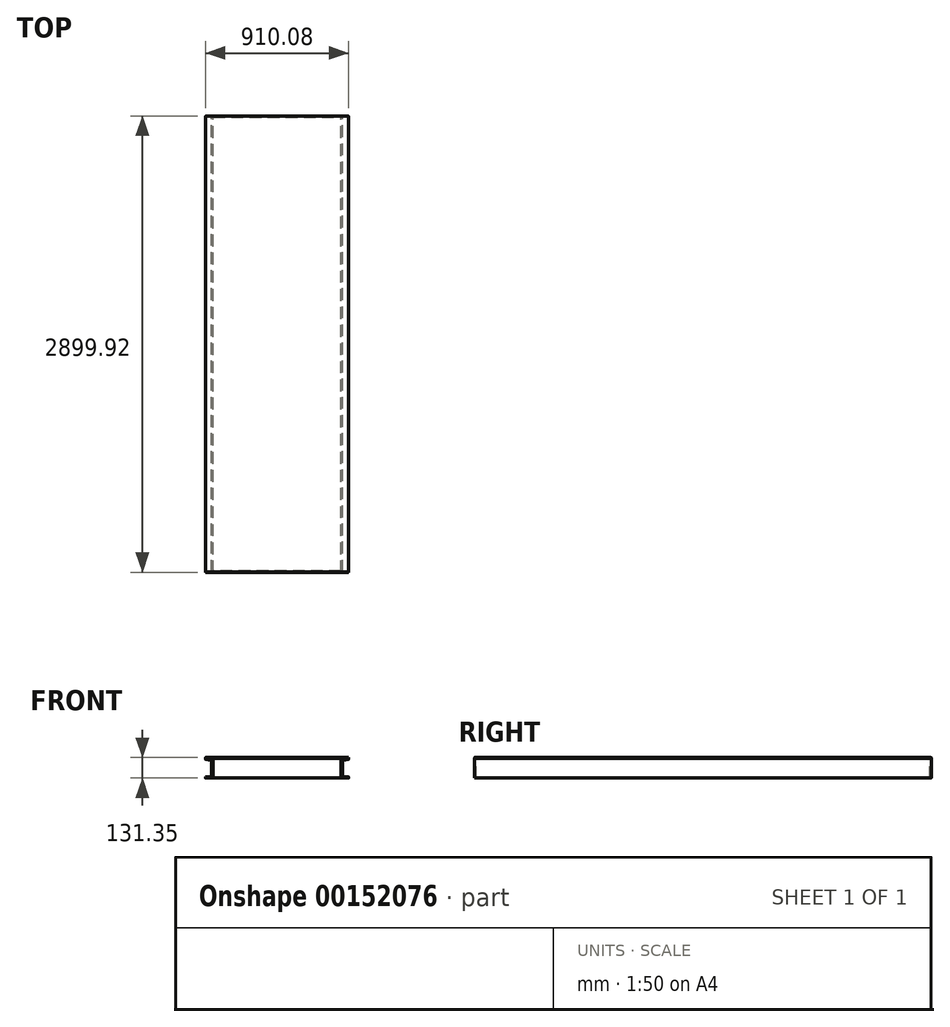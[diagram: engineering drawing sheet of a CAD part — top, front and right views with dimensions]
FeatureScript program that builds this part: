
annotation { "Feature Type Name" : "Feature", "Feature Type Description" : "" }
export const myFeature = defineFeature(function(context is Context, id is Id, definition is map)
    precondition{}
    {
        {
            var Q0;
            Q0=qCreatedBy(makeId("Front.planeOp"),FACE);
            var sketch = newSketch(context, id + "F0", { "sketchPlane" : qUnion([Q0])});
            skLineSegment(sketch, "E0", {"start": v(0, 0) * mm, "end": v(-50, 0) * mm});
            skLineSegment(sketch, "E1", {"start": v(0, 0) * mm, "end": v(0, 125) * mm});
            skLineSegment(sketch, "E2", {"start": v(0, 125) * mm, "end": v(-50, 125) * mm});
            skLineSegment(sketch, "E3", {"start": v(-50, 125) * mm, "end": v(-50, 117.2) * mm});
            skLineSegment(sketch, "E4", {"start": v(-50, 117.2) * mm, "end": v(-10, 113) * mm});
            skLineSegment(sketch, "E5", {"start": v(-10, 113) * mm, "end": v(-10, 12) * mm});
            skLineSegment(sketch, "E6", {"start": v(-50, 0) * mm, "end": v(-50, 7.8) * mm});
            skLineSegment(sketch, "E7", {"start": v(-50, 7.8) * mm, "end": v(-10, 12) * mm});
            skLineSegment(sketch, "E8", {"start": v(405, 151.35) * mm, "end": v(405, -34.02) * mm});
            skLineSegment(sketch, "E9.MirrorCS", {"start": v(860, 125) * mm, "end": v(860, 117.2) * mm});
            skLineSegment(sketch, "E10.MirrorCS", {"start": v(860, 0) * mm, "end": v(860, 7.8) * mm});
            skLineSegment(sketch, "E11.MirrorCS", {"start": v(860, 117.2) * mm, "end": v(820, 113) * mm});
            skLineSegment(sketch, "E12.MirrorCS", {"start": v(860, 7.8) * mm, "end": v(820, 12) * mm});
            skLineSegment(sketch, "E13.MirrorCS", {"start": v(810, 125) * mm, "end": v(860, 125) * mm});
            skLineSegment(sketch, "E14.MirrorCS", {"start": v(810, 0) * mm, "end": v(860, 0) * mm});
            skLineSegment(sketch, "E15.MirrorCS", {"start": v(810, 0) * mm, "end": v(810, 125) * mm});
            skLineSegment(sketch, "E16.MirrorCS", {"start": v(820, 113) * mm, "end": v(820, 12) * mm});
            skSolve(sketch);
        }
        {
            var Q0;
            Q0 = qSketchRegion(id + "F0", true);
            extrude(context, id + "F1", {"entities" : qUnion([Q0]), "depth" : 2899.92 * mm});
        }
        {
            var Q0;
            Q0=makeQuery(id+"F1.opExtrude","SWEPT_FACE",FACE,{"disambiguationData":[OSD([sQuery(id+"F0.wireOp",EDGE,"E2")])]});
            var sketch = newSketch(context, id + "F2", { "sketchPlane" : qUnion([Q0])});
            skLineSegment(sketch, "E17.bottom", {"start": v(-50, 0) * mm, "end": v(860.08, 0) * mm});
            skLineSegment(sketch, "E17.top", {"start": v(-50, -2899.92) * mm, "end": v(860.08, -2899.92) * mm});
            skLineSegment(sketch, "E17.left", {"start": v(-50, 0) * mm, "end": v(-50, -2899.92) * mm});
            skLineSegment(sketch, "E17.right", {"start": v(860.08, 0) * mm, "end": v(860.08, -2899.92) * mm});
            skSolve(sketch);
        }
        {
            var Q0;
            Q0 = qSketchRegion(id + "F2", true);
            extrude(context, id + "F3", {"entities" : qUnion([Q0]), "depth" : 6.35 * mm});
        }
        {
            var Q0;
            Q0=makeQuery(id+"F3.opExtrude","CAP_FACE",FACE,{"disambiguationData":[OSD([sQuery(id+"F2.wireOp",EDGE,"E17.bottom"),sQuery(id+"F2.wireOp",EDGE,"E17.top"),sQuery(id+"F2.wireOp",EDGE,"E17.left"),sQuery(id+"F2.wireOp",EDGE,"E17.right")])],"isStart":true});
            var sketch = newSketch(context, id + "F4", { "sketchPlane" : qUnion([Q0])});
            skLineSegment(sketch, "E18.bottom", {"start": v(810.22, 2899.92) * mm, "end": v(0, 2899.92) * mm});
            skLineSegment(sketch, "E18.top", {"start": v(810.22, 2891.42) * mm, "end": v(0, 2891.42) * mm});
            skLineSegment(sketch, "E18.left", {"start": v(810.22, 2899.92) * mm, "end": v(810.22, 2891.42) * mm});
            skLineSegment(sketch, "E18.right", {"start": v(0, 2899.92) * mm, "end": v(0, 2891.42) * mm});
            skSolve(sketch);
        }
        {
            var Q0;
            Q0 = qSketchRegion(id + "F4", true);
            extrude(context, id + "F5", {"entities" : qUnion([Q0]), "depth" : 125 * mm});
        }
        {
            var Q0;
            Q0=makeQuery(id+"F3.opExtrude","CAP_FACE",FACE,{"disambiguationData":[OSD([sQuery(id+"F2.wireOp",EDGE,"E17.bottom"),sQuery(id+"F2.wireOp",EDGE,"E17.top"),sQuery(id+"F2.wireOp",EDGE,"E17.left"),sQuery(id+"F2.wireOp",EDGE,"E17.right")])],"isStart":true});
            var sketch = newSketch(context, id + "F6", { "sketchPlane" : qUnion([Q0])});
            skLineSegment(sketch, "E19.bottom", {"start": v(0, 0) * mm, "end": v(809.94, 0) * mm});
            skLineSegment(sketch, "E19.top", {"start": v(0, 8.5) * mm, "end": v(809.94, 8.5) * mm});
            skLineSegment(sketch, "E19.left", {"start": v(0, 0) * mm, "end": v(0, 8.5) * mm});
            skLineSegment(sketch, "E19.right", {"start": v(809.94, 0) * mm, "end": v(809.94, 8.5) * mm});
            skSolve(sketch);
        }
        {
            var Q0;
            Q0 = qSketchRegion(id + "F6", true);
            extrude(context, id + "F7", {"entities" : qUnion([Q0]), "depth" : 125 * mm});
        }
        {
            var Q0;
            Q0=makeQuery(id+"F1.opExtrude","SWEPT_EDGE",EDGE,{"disambiguationData":[OSD([sQuery(id+"F0.wireOp",EDGE,"E6"),sQuery(id+"F0.wireOp",EDGE,"E7")])]});
            var Q1;
            Q1=makeQuery(id+"F1.opExtrude","SWEPT_EDGE",EDGE,{"disambiguationData":[OSD([sQuery(id+"F0.wireOp",EDGE,"E3"),sQuery(id+"F0.wireOp",EDGE,"E4")])]});
            var Q2;
            Q2=makeQuery(id+"F1.opExtrude","SWEPT_EDGE",EDGE,{"disambiguationData":[OSD([sQuery(id+"F0.wireOp",EDGE,"E4"),sQuery(id+"F0.wireOp",EDGE,"E5")])]});
            var Q3;
            Q3=makeQuery(id+"F1.opExtrude","SWEPT_EDGE",EDGE,{"disambiguationData":[OSD([sQuery(id+"F0.wireOp",EDGE,"E5"),sQuery(id+"F0.wireOp",EDGE,"E7")])]});
            var Q4;
            Q4=makeQuery(id+"F1.opExtrude","SWEPT_EDGE",EDGE,{"disambiguationData":[OSD([sQuery(id+"F0.wireOp",EDGE,"E9.MirrorCS"),sQuery(id+"F0.wireOp",EDGE,"E11.MirrorCS")])]});
            var Q5;
            Q5=makeQuery(id+"F1.opExtrude","SWEPT_EDGE",EDGE,{"disambiguationData":[OSD([sQuery(id+"F0.wireOp",EDGE,"E11.MirrorCS"),sQuery(id+"F0.wireOp",EDGE,"E16.MirrorCS")])]});
            var Q6;
            Q6=makeQuery(id+"F1.opExtrude","SWEPT_EDGE",EDGE,{"disambiguationData":[OSD([sQuery(id+"F0.wireOp",EDGE,"E12.MirrorCS"),sQuery(id+"F0.wireOp",EDGE,"E16.MirrorCS")])]});
            var Q7;
            Q7=makeQuery(id+"F1.opExtrude","SWEPT_EDGE",EDGE,{"disambiguationData":[OSD([sQuery(id+"F0.wireOp",EDGE,"E10.MirrorCS"),sQuery(id+"F0.wireOp",EDGE,"E12.MirrorCS")])]});
            fillet(context, id + "F8", {"entities" : qUnion([Q0, Q1, Q2, Q3, Q4, Q5, Q6, Q7]), "radius" : 3 * mm, "tangentPropagation" : true, "allowEdgeOverflow" : false});
        }
        {
            var Q0;
            Q0=makeQuery(id+"F3.opExtrude","SWEPT_EDGE",EDGE,{"disambiguationData":[OSD([sQuery(id+"F2.wireOp",EDGE,"E17.bottom"),sQuery(id+"F2.wireOp",EDGE,"E17.right")])]});
            var Q1;
            Q1=makeQuery(id+"F1.opExtrude","CAP_EDGE",EDGE,{"disambiguationData":[OSD([sQuery(id+"F0.wireOp",EDGE,"E9.MirrorCS")])],"isStart":true});
            var Q2;
            Q2=makeQuery(id+"F3.opExtrude","SWEPT_EDGE",EDGE,{"disambiguationData":[OSD([sQuery(id+"F2.wireOp",EDGE,"E17.bottom"),sQuery(id+"F2.wireOp",EDGE,"E17.left")])]});
            var Q3;
            Q3=makeQuery(id+"F1.opExtrude","CAP_EDGE",EDGE,{"disambiguationData":[OSD([sQuery(id+"F0.wireOp",EDGE,"E3")])],"isStart":true});
            var Q4;
            Q4=makeQuery(id+"F3.opExtrude","SWEPT_EDGE",EDGE,{"disambiguationData":[OSD([sQuery(id+"F2.wireOp",EDGE,"E17.top"),sQuery(id+"F2.wireOp",EDGE,"E17.left")])]});
            var Q5;
            Q5=makeQuery(id+"F1.opExtrude","CAP_EDGE",EDGE,{"disambiguationData":[OSD([sQuery(id+"F0.wireOp",EDGE,"E3")])],"isStart":false});
            var Q6;
            Q6=makeQuery(id+"F3.opExtrude","SWEPT_EDGE",EDGE,{"disambiguationData":[OSD([sQuery(id+"F2.wireOp",EDGE,"E17.top"),sQuery(id+"F2.wireOp",EDGE,"E17.right")])]});
            var Q7;
            Q7=makeQuery(id+"F1.opExtrude","CAP_EDGE",EDGE,{"disambiguationData":[OSD([sQuery(id+"F0.wireOp",EDGE,"E9.MirrorCS")])],"isStart":false});
            fillet(context, id + "F9", {"entities" : qUnion([Q0, Q1, Q2, Q3, Q4, Q5, Q6, Q7]), "radius" : 5 * mm, "tangentPropagation" : true, "allowEdgeOverflow" : false});
        }
        {
            var Q0;
            Q0=makeQuery(id+"F3.opExtrude","CAP_EDGE",EDGE,{"disambiguationData":[OSD([sQuery(id+"F2.wireOp",EDGE,"E17.top")])],"isStart":false});
            chamfer(context, id + "F10", {"entities" : qUnion([Q0]), "width" : 2 * mm, "tangentPropagation" : true});
        }
    });
